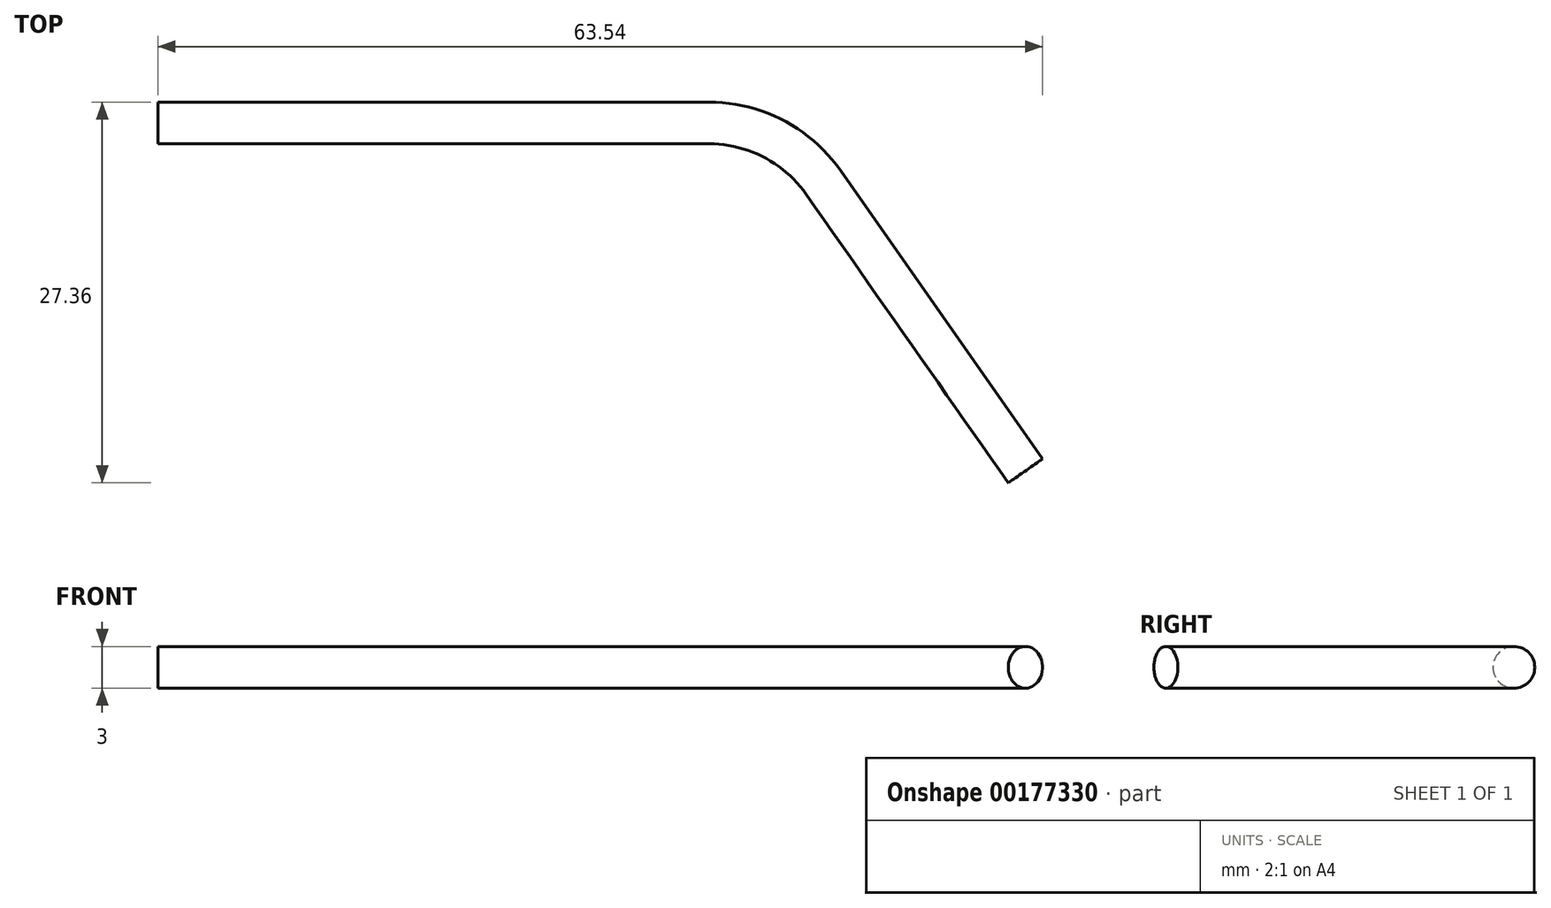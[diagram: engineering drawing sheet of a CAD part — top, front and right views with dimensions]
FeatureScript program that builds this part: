
annotation { "Feature Type Name" : "Feature", "Feature Type Description" : "" }
export const myFeature = defineFeature(function(context is Context, id is Id, definition is map)
    precondition{}
    {
        {
            var Q0;
            Q0=qCreatedBy(makeId("Top.planeOp"),FACE);
            var sketch = newSketch(context, id + "F0", { "sketchPlane" : qUnion([Q0])});
            skLineSegment(sketch, "E0", {"start": v(0, 0) * mm, "end": v(-14.52, 20.74) * mm});
            skLineSegment(sketch, "E1", {"start": v(-22.71, 25) * mm, "end": v(-62.3, 25) * mm});
            skPoint(sketch, "E2.visualSharp", {"position": v(-17.5, 25) * mm});
            skArc(sketch, "E2.filletArc", {"start": v(-14.52, 20.74) * mm, "mid": v(-18.1, 23.87) * mm, "end": v(-22.71, 25) * mm});
            skSolve(sketch);
        }
        {
            var Q0;
            Q0=qCreatedBy(makeId("Top.planeOp"),FACE);
            var sketch = newSketch(context, id + "F1", { "sketchPlane" : qUnion([Q0])});
            skLineSegment(sketch, "E3", {"start": v(-31.75, -22.23) * mm, "end": v(29.07, 20.36) * mm});
            skSolve(sketch);
        }
        {
            var Q0;
            Q0=sQuery(id+"F1.wireOp",EDGE,"E3");
            cPlane(context, id + "F2", {"entities" : qUnion([Q0]), "cplaneType" : CPlaneType.LINE_ANGLE, "offset" : 25 * mm, "angle" : 0 * degree, "width" : 150 * mm, "height" : 150 * mm});
        }
        {
            var Q0;
            Q0=qCreatedBy(id+"F2.planeOp",FACE);
            var sketch = newSketch(context, id + "F3", { "sketchPlane" : qUnion([Q0])});
            skCircle(sketch, "E4", {"center": v(0, 0) * mm, "radius": 1.5 * mm});
            skSolve(sketch);
        }
        {
            var Q0;
            Q0=makeQuery(id+"F3.imprint","IMPRINT",FACE,{"disambiguationData":[TD([[makeQuery(id+"F3.imprint","IMPRINT",EDGE,{"derivedFrom":sQuery(id+"F3.wireOp",EDGE,"E4")}),1.0]])]});
            var Q1;
            Q1=sQuery(id+"F0.wireOp",EDGE,"E0");
            var Q2;
            Q2=sQuery(id+"F0.wireOp",EDGE,"E2.filletArc");
            var Q3;
            Q3=sQuery(id+"F0.wireOp",EDGE,"E1");
            sweep(context, id + "F4", {"profiles" : qUnion([Q0]), "path" : qUnion([Q1, Q2, Q3])});
        }
    });
